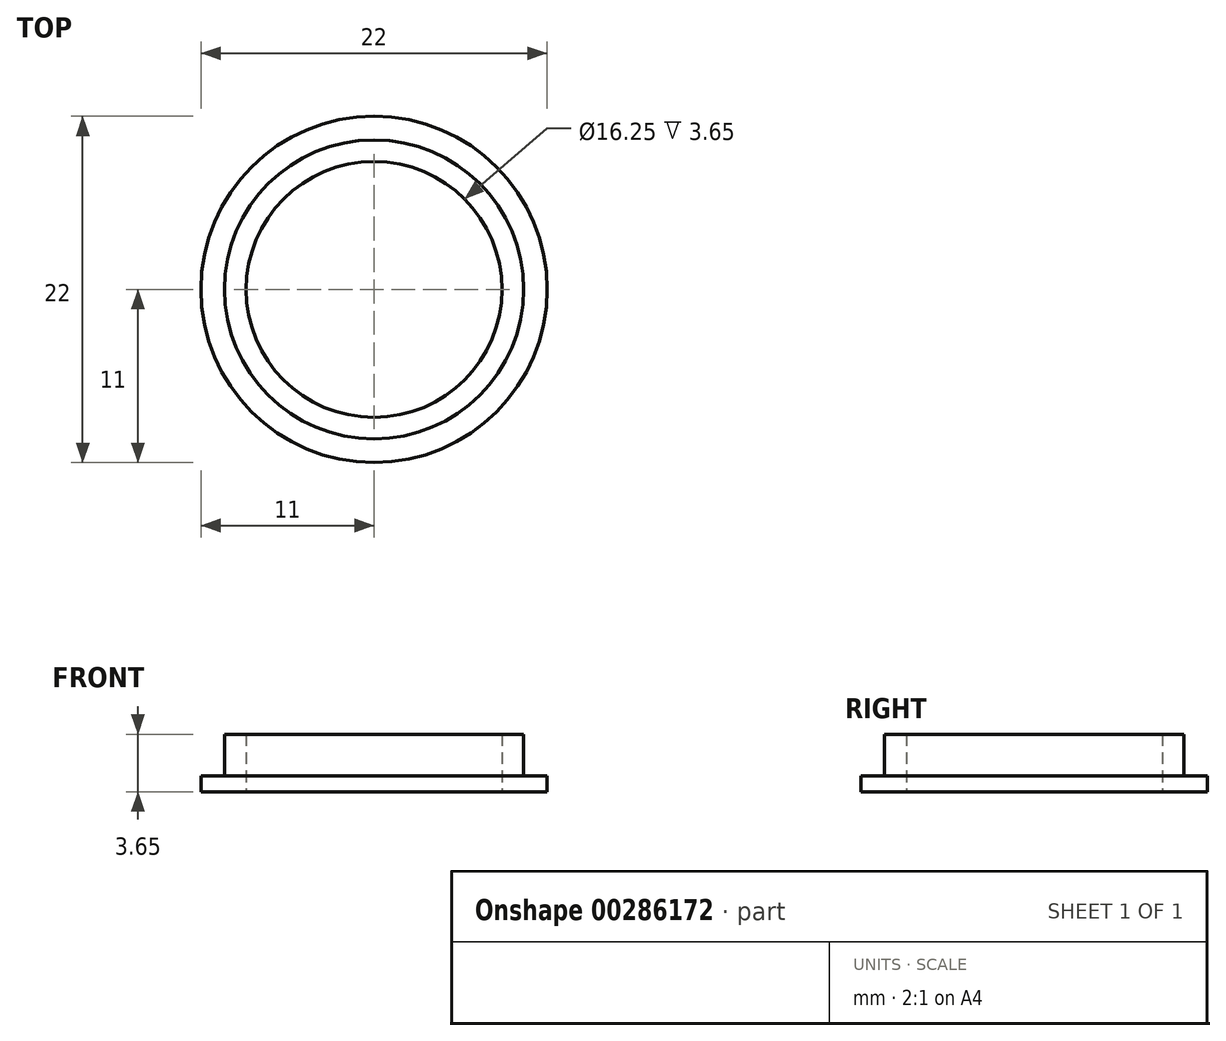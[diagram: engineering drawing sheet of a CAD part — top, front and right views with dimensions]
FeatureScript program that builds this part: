
annotation { "Feature Type Name" : "Feature", "Feature Type Description" : "" }
export const myFeature = defineFeature(function(context is Context, id is Id, definition is map)
    precondition{}
    {
        {
            var Q0;
            Q0=qCreatedBy(makeId("Top.planeOp"),FACE);
            var sketch = newSketch(context, id + "F0", { "sketchPlane" : qUnion([Q0])});
            skCircle(sketch, "E0", {"center": v(0, 0) * mm, "radius": 8.12 * mm});
            skCircle(sketch, "E1", {"center": v(0, 0) * mm, "radius": 11 * mm});
            skCircle(sketch, "E2", {"center": v(0, 0) * mm, "radius": 9.5 * mm});
            skSolve(sketch);
        }
        {
            var Q0;
            Q0=makeQuery(id+"F0.imprint","IMPRINT",FACE,{"disambiguationData":[TD([[makeQuery(id+"F0.imprint","IMPRINT",EDGE,{"derivedFrom":sQuery(id+"F0.wireOp",EDGE,"E0")}),-1.0]])]});
            extrude(context, id + "F1", {"entities" : qUnion([Q0]), "depth" : (3.6 - 0.95) * mm});
        }
        {
            var Q0;
            Q0=makeQuery(id+"F0.imprint","IMPRINT",FACE,{"disambiguationData":[TD([[makeQuery(id+"F0.imprint","IMPRINT",EDGE,{"derivedFrom":sQuery(id+"F0.wireOp",EDGE,"E0")}),-1.0]])]});
            var Q1;
            Q1=makeQuery(id+"F0.imprint","IMPRINT",FACE,{"disambiguationData":[TD([[makeQuery(id+"F0.imprint","IMPRINT",EDGE,{"derivedFrom":sQuery(id+"F0.wireOp",EDGE,"E1")}),1.0]])]});
            extrude(context, id + "F2", {"entities" : qUnion([Q0, Q1]), "operationType" : NewBodyOperationType.ADD, "oppositeDirection" : true, "depth" : 1 * mm});
        }
    });
